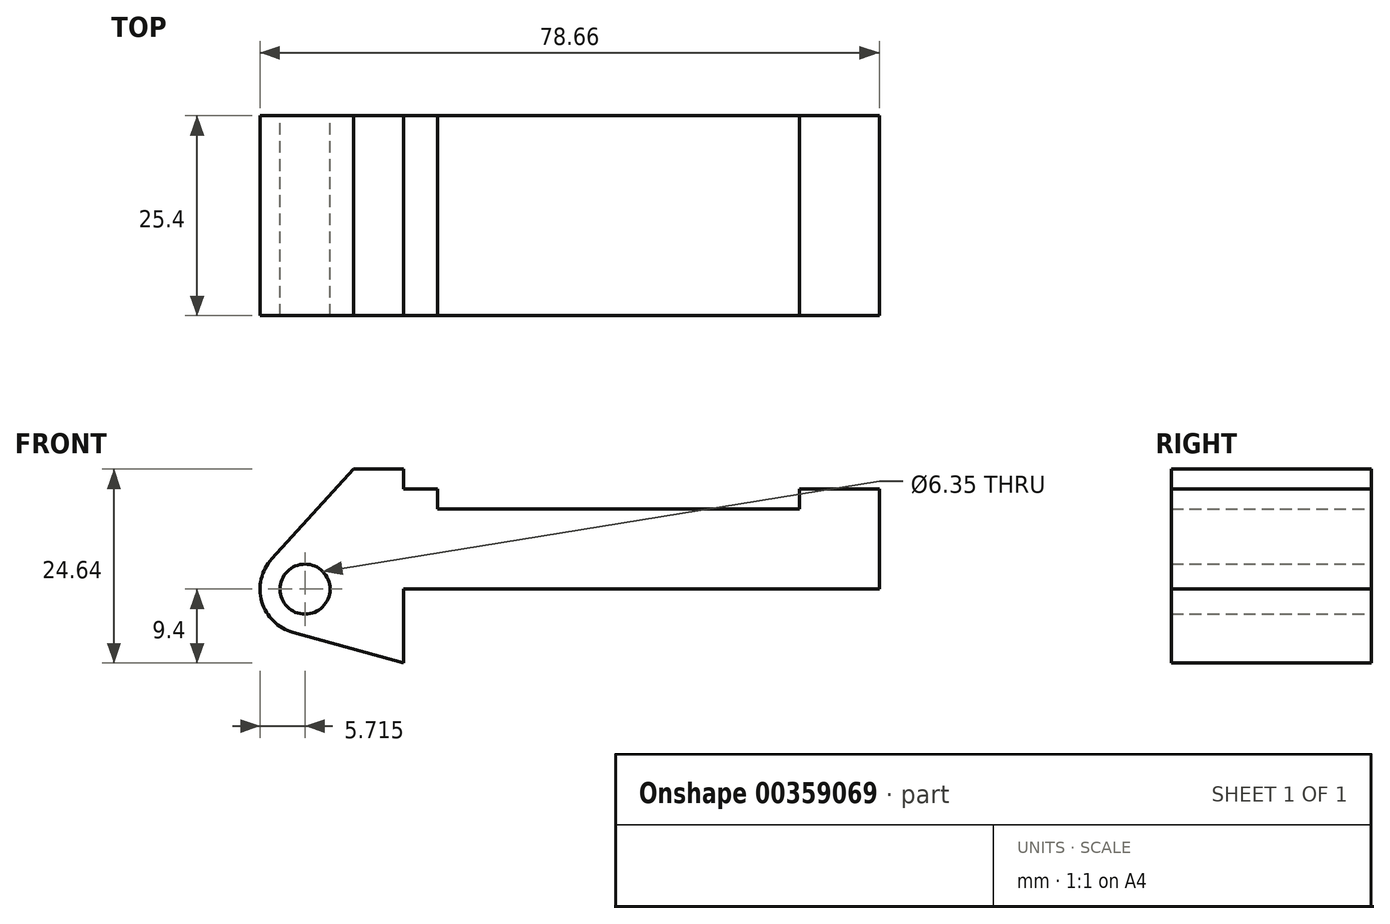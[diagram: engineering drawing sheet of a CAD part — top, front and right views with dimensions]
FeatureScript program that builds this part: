
annotation { "Feature Type Name" : "Feature", "Feature Type Description" : "" }
export const myFeature = defineFeature(function(context is Context, id is Id, definition is map)
    precondition{}
    {
        {
            var Q0;
            Q0=qCreatedBy(makeId("Front.planeOp"),FACE);
            var sketch = newSketch(context, id + "F0", { "sketchPlane" : qUnion([Q0])});
            skLineSegment(sketch, "E0", {"start": v(0, 0) * mm, "end": v(0, 12.7) * mm});
            skLineSegment(sketch, "E1", {"start": v(0, 12.7) * mm, "end": v(10.16, 12.7) * mm});
            skLineSegment(sketch, "E2", {"start": v(10.16, 12.7) * mm, "end": v(10.16, 10.16) * mm});
            skLineSegment(sketch, "E3", {"start": v(10.16, 10.16) * mm, "end": v(56.13, 10.16) * mm});
            skLineSegment(sketch, "E4", {"start": v(56.13, 10.16) * mm, "end": v(56.13, 12.7) * mm});
            skLineSegment(sketch, "E5", {"start": v(56.13, 12.7) * mm, "end": v(66.3, 12.7) * mm});
            skLineSegment(sketch, "E6", {"start": v(66.3, 12.7) * mm, "end": v(66.3, 0) * mm});
            skLineSegment(sketch, "E7", {"start": v(66.3, 0) * mm, "end": v(0, 0) * mm});
            skLineSegment(sketch, "E8", {"start": v(5.84, 15.24) * mm, "end": v(-0.5, 15.24) * mm});
            skLineSegment(sketch, "E9", {"start": v(-0.5, 15.24) * mm, "end": v(-10.88, 3.85) * mm});
            skLineSegment(sketch, "E10", {"start": v(0, 0) * mm, "end": v(-6.65, 0) * mm});
            skCircle(sketch, "E11", {"center": v(-6.65, 0) * mm, "radius": 5.72 * mm});
            skCircle(sketch, "E12", {"center": v(-6.65, 0) * mm, "radius": 3.18 * mm});
            skLineSegment(sketch, "E13", {"start": v(5.84, 15.24) * mm, "end": v(5.84, -9.4) * mm});
            skLineSegment(sketch, "E14", {"start": v(5.84, -9.4) * mm, "end": v(-8.18, -5.5) * mm});
            skSolve(sketch);
        }
        {
            var Q0;
            {var subQ1=sQuery(id+"F0.wireOp",EDGE,"E0");Q0=makeQuery(id+"F0.imprint","IMPRINT",FACE,{"disambiguationData":[TD([[makeQuery(id+"F0.imprint","IMPRINT",EDGE,{"derivedFrom":subQ1}),1.0]])]});}
            var Q1;
            {var subQ5=sQuery(id+"F0.wireOp",EDGE,"E12");Q1=makeQuery(id+"F0.imprint","IMPRINT",FACE,{"disambiguationData":[TD([[makeQuery(id+"F0.imprint","IMPRINT",EDGE,{"derivedFrom":subQ5}),-1.0]])]});}
            var Q2;
            {var subQ0=sQuery(id+"F0.wireOp",EDGE,"E14");Q2=makeQuery(id+"F0.imprint","IMPRINT",FACE,{"disambiguationData":[TD([[makeQuery(id+"F0.imprint","IMPRINT",EDGE,{"derivedFrom":subQ0}),-1.0]])]});}
            var Q3;
            {var subQ0=sQuery(id+"F0.wireOp",EDGE,"E0");Q3=makeQuery(id+"F0.imprint","IMPRINT",FACE,{"disambiguationData":[TD([[makeQuery(id+"F0.imprint","IMPRINT",EDGE,{"derivedFrom":subQ0}),-1.0]])]});}
            var Q4;
            {var subQ0=sQuery(id+"F0.wireOp",EDGE,"E2");Q4=makeQuery(id+"F0.imprint","IMPRINT",FACE,{"disambiguationData":[TD([[makeQuery(id+"F0.imprint","IMPRINT",EDGE,{"derivedFrom":subQ0}),-1.0]])]});}
            extrude(context, id + "F1", {"entities" : qUnion([Q0, Q1, Q2, Q3, Q4]), "depth" : 25.4 * mm});
        }
    });
